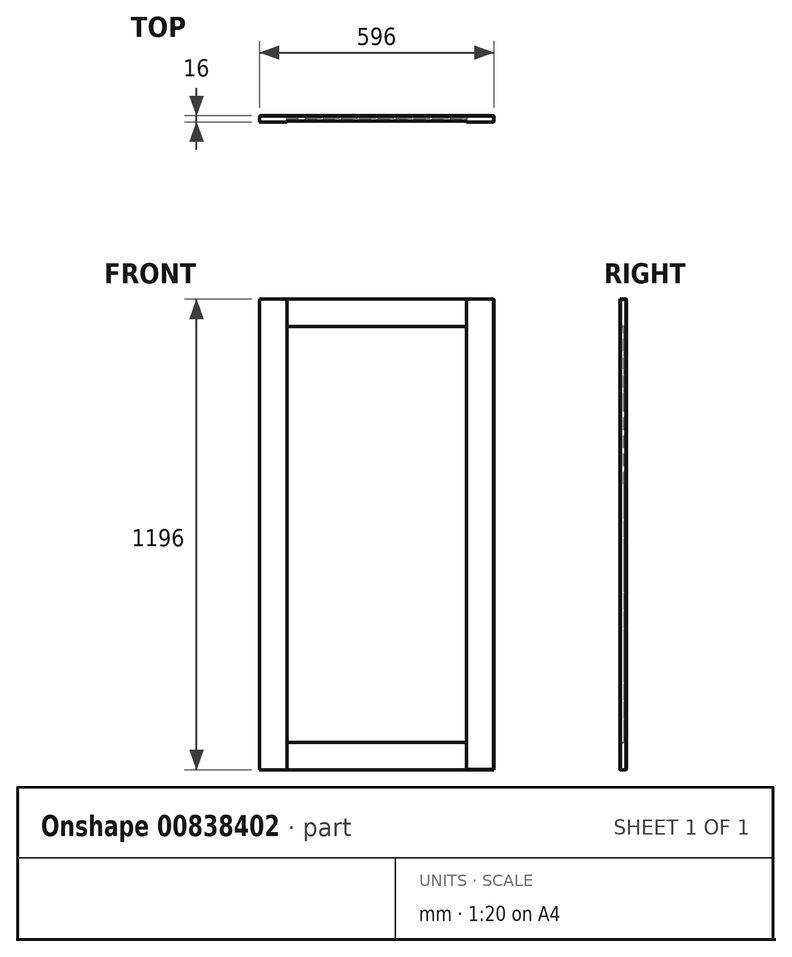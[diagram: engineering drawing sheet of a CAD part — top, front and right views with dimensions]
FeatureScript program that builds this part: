
annotation { "Feature Type Name" : "Feature", "Feature Type Description" : "" }
export const myFeature = defineFeature(function(context is Context, id is Id, definition is map)
    precondition{}
    {
        {
            var Q0;
            Q0=qCreatedBy(makeId("Front.planeOp"),FACE);
            var sketch = newSketch(context, id + "F0", { "sketchPlane" : qUnion([Q0])});
            skLineSegment(sketch, "E0.bottom", {"start": v(0, 0) * mm, "end": v(35.9, 0) * mm});
            skLineSegment(sketch, "E0.top", {"start": v(0, 30.12) * mm, "end": v(35.9, 30.12) * mm});
            skLineSegment(sketch, "E0.left", {"start": v(0, 0) * mm, "end": v(0, 30.12) * mm});
            skLineSegment(sketch, "E0.right", {"start": v(35.9, 0) * mm, "end": v(35.9, 30.12) * mm});
            skSolve(sketch);
        }
        {
            var Q0;
            Q0=makeQuery(id+"F0.imprint","IMPRINT",FACE,{"disambiguationData":[TD([[makeQuery(id+"F0.imprint","IMPRINT",EDGE,{"derivedFrom":sQuery(id+"F0.wireOp",EDGE,"E0.bottom")}),1.0]])]});
            extrude(context, id + "F1", {"entities" : qUnion([Q0]), "depth" : 16 * mm, "offsetDistance" : 25.4 * mm});
        }
        {
            var Q0;
            Q0=makeQuery(id+"F1.opExtrude","SWEPT_FACE",FACE,{"disambiguationData":[OSD([sQuery(id+"F0.wireOp",EDGE,"E0.left")])]});
            extrude(context, id + "F2", {"entities" : qUnion([Q0]), "operationType" : NewBodyOperationType.ADD, "oppositeDirection" : true, "depth" : 196 * mm, "offsetDistance" : 25 * mm});
        }
        {
            var Q0;
            {var subQ0=sQuery(id+"F0.wireOp",EDGE,"E0.bottom");Q0=makeQuery(id+"F2.boolean.opBoolean","MERGE",FACE,{"derivedFrom":[makeQuery(id+"F1.opExtrude","SWEPT_FACE",FACE,{"disambiguationData":[OSD([subQ0])]}),makeQuery(id+"F2.opExtrude","SWEPT_FACE",FACE,{"disambiguationData":[OSD([subQ0,sQuery(id+"F0.wireOp",EDGE,"E0.left")])]})]});}
            extrude(context, id + "F3", {"entities" : qUnion([Q0]), "operationType" : NewBodyOperationType.ADD, "oppositeDirection" : true, "depth" : 796 * mm, "offsetDistance" : 25 * mm});
        }
        {
            var Q0;
            {var subQ0=sQuery(id+"F0.wireOp",EDGE,"E0.left");var subQ1=sQuery(id+"F0.wireOp",EDGE,"E0.bottom");Q0=makeQuery(id+"F3.boolean.opBoolean","MERGE",FACE,{"derivedFrom":[makeQuery(id+"F2.boolean.opBoolean","MERGE",FACE,{"derivedFrom":[makeQuery(id+"F1.opExtrude","CAP_FACE",FACE,{"disambiguationData":[OSD([subQ1,sQuery(id+"F0.wireOp",EDGE,"E0.top"),subQ0,sQuery(id+"F0.wireOp",EDGE,"E0.right")])],"isStart":false}),makeQuery(id+"F2.opExtrude","SWEPT_FACE",FACE,{"disambiguationData":[OSD([subQ0]),TDD([makeQuery(id+"F1.opExtrude","CAP_EDGE",EDGE,{"disambiguationData":[OSD([subQ0])],"isStart":false})])]})]}),makeQuery(id+"F3.opExtrude","SWEPT_FACE",FACE,{"disambiguationData":[OSD([subQ1,subQ0]),TDD([makeQuery(id+"F2.boolean.opBoolean","MERGE",EDGE,{"derivedFrom":[makeQuery(id+"F1.opExtrude","CAP_EDGE",EDGE,{"disambiguationData":[OSD([subQ1])],"isStart":false}),makeQuery(id+"F2.opExtrude","SWEPT_EDGE",EDGE,{"disambiguationData":[OSD([subQ1,subQ0]),TDD([makeQuery(id+"F1.opExtrude","CAP_VERTEX",VERTEX,{"disambiguationData":[OSD([subQ1,subQ0])],"isStart":false})])]})]})])]})]});}
            var sketch = newSketch(context, id + "F4", { "sketchPlane" : qUnion([Q0])});
            skLineSegment(sketch, "E1.bottom", {"start": v(0, 796) * mm, "end": v(42.19, 796) * mm});
            skLineSegment(sketch, "E1.top", {"start": v(0, 751.57) * mm, "end": v(42.19, 751.57) * mm});
            skLineSegment(sketch, "E1.left", {"start": v(0, 796) * mm, "end": v(0, 751.57) * mm});
            skLineSegment(sketch, "E1.right", {"start": v(42.19, 796) * mm, "end": v(42.19, 751.57) * mm});
            skLineSegment(sketch, "E2.bottom", {"start": v(196, 796) * mm, "end": v(153.6, 796) * mm});
            skLineSegment(sketch, "E2.top", {"start": v(196, 746.75) * mm, "end": v(153.6, 746.75) * mm});
            skLineSegment(sketch, "E2.left", {"start": v(196, 796) * mm, "end": v(196, 746.75) * mm});
            skLineSegment(sketch, "E2.right", {"start": v(153.6, 796) * mm, "end": v(153.6, 746.75) * mm});
            skSolve(sketch);
        }
        {
            var Q0;
            Q0=makeQuery(id+"F4.imprint","IMPRINT",FACE,{"disambiguationData":[TD([[makeQuery(id+"F4.imprint","IMPRINT",EDGE,{"derivedFrom":sQuery(id+"F4.wireOp",EDGE,"E1.bottom")}),-1.0]])]});
            var Q1;
            Q1=makeQuery(id+"F4.imprint","IMPRINT",FACE,{"disambiguationData":[TD([[makeQuery(id+"F4.imprint","IMPRINT",EDGE,{"derivedFrom":sQuery(id+"F4.wireOp",EDGE,"E2.bottom")}),-1.0]])]});
            extrude(context, id + "F5", {"entities" : qUnion([Q0, Q1]), "operationType" : NewBodyOperationType.ADD, "depth" : 25 * mm, "offsetDistance" : 25 * mm});
        }
        {
            var Q0;
            {var subQ0=sQuery(id+"F0.wireOp",EDGE,"E0.left");var subQ1=sQuery(id+"F0.wireOp",EDGE,"E0.bottom");Q0=makeQuery(id+"F3.boolean.opBoolean","MERGE",FACE,{"derivedFrom":[makeQuery(id+"F2.boolean.opBoolean","MERGE",FACE,{"derivedFrom":[makeQuery(id+"F1.opExtrude","CAP_FACE",FACE,{"disambiguationData":[OSD([subQ1,sQuery(id+"F0.wireOp",EDGE,"E0.top"),subQ0,sQuery(id+"F0.wireOp",EDGE,"E0.right")])],"isStart":false}),makeQuery(id+"F2.opExtrude","SWEPT_FACE",FACE,{"disambiguationData":[OSD([subQ0]),TDD([makeQuery(id+"F1.opExtrude","CAP_EDGE",EDGE,{"disambiguationData":[OSD([subQ0])],"isStart":false})])]})]}),makeQuery(id+"F3.opExtrude","SWEPT_FACE",FACE,{"disambiguationData":[OSD([subQ1,subQ0]),TDD([makeQuery(id+"F2.boolean.opBoolean","MERGE",EDGE,{"derivedFrom":[makeQuery(id+"F1.opExtrude","CAP_EDGE",EDGE,{"disambiguationData":[OSD([subQ1])],"isStart":false}),makeQuery(id+"F2.opExtrude","SWEPT_EDGE",EDGE,{"disambiguationData":[OSD([subQ1,subQ0]),TDD([makeQuery(id+"F1.opExtrude","CAP_VERTEX",VERTEX,{"disambiguationData":[OSD([subQ1,subQ0])],"isStart":false})])]})]})])]})]});}
            var sketch = newSketch(context, id + "F6", { "sketchPlane" : qUnion([Q0])});
            skLineSegment(sketch, "E3.bottom", {"start": v(196, 0) * mm, "end": v(163.38, 0) * mm});
            skLineSegment(sketch, "E3.top", {"start": v(196, 46.55) * mm, "end": v(163.38, 46.55) * mm});
            skLineSegment(sketch, "E3.left", {"start": v(196, 0) * mm, "end": v(196, 46.55) * mm});
            skLineSegment(sketch, "E3.right", {"start": v(163.38, 0) * mm, "end": v(163.38, 46.55) * mm});
            skLineSegment(sketch, "E4.bottom", {"start": v(0, 0) * mm, "end": v(50.28, 0) * mm});
            skLineSegment(sketch, "E4.top", {"start": v(0, 44.4) * mm, "end": v(50.28, 44.4) * mm});
            skLineSegment(sketch, "E4.left", {"start": v(0, 0) * mm, "end": v(0, 44.4) * mm});
            skLineSegment(sketch, "E4.right", {"start": v(50.28, 0) * mm, "end": v(50.28, 44.4) * mm});
            skSolve(sketch);
        }
        {
            var Q0;
            Q0=makeQuery(id+"F6.imprint","IMPRINT",FACE,{"disambiguationData":[TD([[makeQuery(id+"F6.imprint","IMPRINT",EDGE,{"derivedFrom":sQuery(id+"F6.wireOp",EDGE,"E3.bottom")}),1.0]])]});
            var Q1;
            Q1=makeQuery(id+"F6.imprint","IMPRINT",FACE,{"disambiguationData":[TD([[makeQuery(id+"F6.imprint","IMPRINT",EDGE,{"derivedFrom":sQuery(id+"F6.wireOp",EDGE,"E4.bottom")}),1.0]])]});
            extrude(context, id + "F7", {"entities" : qUnion([Q0, Q1]), "operationType" : NewBodyOperationType.ADD, "depth" : 25 * mm, "offsetDistance" : 25 * mm});
        }
        {
            var Q0;
            Q0=makeQuery(id+"F7.opExtrude","SWEPT_FACE",FACE,{"disambiguationData":[OSD([sQuery(id+"F6.wireOp",EDGE,"E4.right")])]});
            extrude(context, id + "F8", {"entities" : qUnion([Q0]), "operationType" : NewBodyOperationType.ADD, "depth" : 19.72 * mm, "offsetDistance" : 25 * mm});
        }
        {
            var Q0;
            {var subQ0=sQuery(id+"F6.wireOp",EDGE,"E4.top");Q0=makeQuery(id+"F8.boolean.opBoolean","MERGE",FACE,{"derivedFrom":[makeQuery(id+"F7.opExtrude","SWEPT_FACE",FACE,{"disambiguationData":[OSD([subQ0])]}),makeQuery(id+"F8.opExtrude","SWEPT_FACE",FACE,{"disambiguationData":[OSD([subQ0,sQuery(id+"F6.wireOp",EDGE,"E4.right")])]})]});}
            extrude(context, id + "F9", {"entities" : qUnion([Q0]), "operationType" : NewBodyOperationType.ADD, "depth" : 25.6 * mm, "offsetDistance" : 25 * mm});
        }
        {
            var Q0;
            Q0=makeQuery(id+"F7.opExtrude","SWEPT_FACE",FACE,{"disambiguationData":[OSD([sQuery(id+"F6.wireOp",EDGE,"E3.right")])]});
            extrude(context, id + "F10", {"entities" : qUnion([Q0]), "operationType" : NewBodyOperationType.ADD, "depth" : 37.38 * mm, "offsetDistance" : 25 * mm});
        }
        {
            var Q0;
            {var subQ0=sQuery(id+"F6.wireOp",EDGE,"E3.top");Q0=makeQuery(id+"F10.boolean.opBoolean","MERGE",FACE,{"derivedFrom":[makeQuery(id+"F7.opExtrude","SWEPT_FACE",FACE,{"disambiguationData":[OSD([subQ0])]}),makeQuery(id+"F10.opExtrude","SWEPT_FACE",FACE,{"disambiguationData":[OSD([subQ0,sQuery(id+"F6.wireOp",EDGE,"E3.right")])]})]});}
            extrude(context, id + "F11", {"entities" : qUnion([Q0]), "operationType" : NewBodyOperationType.ADD, "depth" : 23.45 * mm, "offsetDistance" : 25 * mm});
        }
        {
            var Q0;
            Q0=makeQuery(id+"F5.opExtrude","SWEPT_FACE",FACE,{"disambiguationData":[OSD([sQuery(id+"F4.wireOp",EDGE,"E1.right")])]});
            extrude(context, id + "F12", {"entities" : qUnion([Q0]), "operationType" : NewBodyOperationType.ADD, "depth" : 27.8 * mm, "offsetDistance" : 25 * mm});
        }
        {
            var Q0;
            {var subQ0=sQuery(id+"F4.wireOp",EDGE,"E1.top");Q0=makeQuery(id+"F12.boolean.opBoolean","MERGE",FACE,{"derivedFrom":[makeQuery(id+"F5.opExtrude","SWEPT_FACE",FACE,{"disambiguationData":[OSD([subQ0])]}),makeQuery(id+"F12.opExtrude","SWEPT_FACE",FACE,{"disambiguationData":[OSD([subQ0,sQuery(id+"F4.wireOp",EDGE,"E1.right")])]})]});}
            extrude(context, id + "F13", {"entities" : qUnion([Q0]), "operationType" : NewBodyOperationType.ADD, "depth" : 25.57 * mm, "offsetDistance" : 25 * mm});
        }
        {
            var Q0;
            Q0=makeQuery(id+"F5.opExtrude","SWEPT_FACE",FACE,{"disambiguationData":[OSD([sQuery(id+"F4.wireOp",EDGE,"E2.top")])]});
            extrude(context, id + "F14", {"entities" : qUnion([Q0]), "operationType" : NewBodyOperationType.ADD, "depth" : 20.75 * mm, "offsetDistance" : 25 * mm});
        }
        {
            var Q0;
            {var subQ0=sQuery(id+"F4.wireOp",EDGE,"E2.right");Q0=makeQuery(id+"F14.boolean.opBoolean","MERGE",FACE,{"derivedFrom":[makeQuery(id+"F5.opExtrude","SWEPT_FACE",FACE,{"disambiguationData":[OSD([subQ0])]}),makeQuery(id+"F14.opExtrude","SWEPT_FACE",FACE,{"disambiguationData":[OSD([sQuery(id+"F4.wireOp",EDGE,"E2.top"),subQ0])]})]});}
            extrude(context, id + "F15", {"entities" : qUnion([Q0]), "operationType" : NewBodyOperationType.ADD, "depth" : 27.6 * mm, "offsetDistance" : 25 * mm});
        }
        {
            var Q0;
            {var subQ0=sQuery(id+"F0.wireOp",EDGE,"E0.left");var subQ1=sQuery(id+"F0.wireOp",EDGE,"E0.bottom");Q0=makeQuery(id+"F3.boolean.opBoolean","MERGE",FACE,{"derivedFrom":[makeQuery(id+"F2.boolean.opBoolean","MERGE",FACE,{"derivedFrom":[makeQuery(id+"F1.opExtrude","CAP_FACE",FACE,{"disambiguationData":[OSD([subQ1,sQuery(id+"F0.wireOp",EDGE,"E0.top"),subQ0,sQuery(id+"F0.wireOp",EDGE,"E0.right")])],"isStart":false}),makeQuery(id+"F2.opExtrude","SWEPT_FACE",FACE,{"disambiguationData":[OSD([subQ0]),TDD([makeQuery(id+"F1.opExtrude","CAP_EDGE",EDGE,{"disambiguationData":[OSD([subQ0])],"isStart":false})])]})]}),makeQuery(id+"F3.opExtrude","SWEPT_FACE",FACE,{"disambiguationData":[OSD([subQ1,subQ0]),TDD([makeQuery(id+"F2.boolean.opBoolean","MERGE",EDGE,{"derivedFrom":[makeQuery(id+"F1.opExtrude","CAP_EDGE",EDGE,{"disambiguationData":[OSD([subQ1])],"isStart":false}),makeQuery(id+"F2.opExtrude","SWEPT_EDGE",EDGE,{"disambiguationData":[OSD([subQ1,subQ0]),TDD([makeQuery(id+"F1.opExtrude","CAP_VERTEX",VERTEX,{"disambiguationData":[OSD([subQ1,subQ0])],"isStart":false})])]})]})])]})]});}
            var sketch = newSketch(context, id + "F16", { "sketchPlane" : qUnion([Q0])});
            skLineSegment(sketch, "E5.bottom", {"start": v(70, 726) * mm, "end": v(126, 726) * mm});
            skLineSegment(sketch, "E5.top", {"start": v(70, 70) * mm, "end": v(126, 70) * mm});
            skLineSegment(sketch, "E5.left", {"start": v(70, 726) * mm, "end": v(70, 70) * mm});
            skLineSegment(sketch, "E5.right", {"start": v(126, 726) * mm, "end": v(126, 70) * mm});
            skSolve(sketch);
        }
        {
            var Q0;
            Q0=makeQuery(id+"F16.imprint","IMPRINT",FACE,{"disambiguationData":[TD([[makeQuery(id+"F16.imprint","IMPRINT",EDGE,{"derivedFrom":sQuery(id+"F16.wireOp",EDGE,"E5.top")}),1.0]])]});
            extrude(context, id + "F17", {"entities" : qUnion([Q0]), "operationType" : NewBodyOperationType.REMOVE, "oppositeDirection" : true, "depth" : 10 * mm, "offsetDistance" : 25 * mm});
        }
        {
            var Q0;
            {var subQ2=sQuery(id+"F0.wireOp",EDGE,"E0.left");var subQ3=sQuery(id+"F0.wireOp",EDGE,"E0.bottom");var subQ4=makeQuery(id+"F1.opExtrude","CAP_FACE",FACE,{"disambiguationData":[OSD([subQ3,sQuery(id+"F0.wireOp",EDGE,"E0.top"),subQ2,sQuery(id+"F0.wireOp",EDGE,"E0.right")])],"isStart":false});var subQ7=makeQuery(id+"F3.opExtrude","SWEPT_FACE",FACE,{"disambiguationData":[OSD([subQ3,subQ2]),TDD([makeQuery(id+"F2.boolean.opBoolean","MERGE",EDGE,{"derivedFrom":[makeQuery(id+"F1.opExtrude","CAP_EDGE",EDGE,{"disambiguationData":[OSD([subQ3])],"isStart":false}),makeQuery(id+"F2.opExtrude","SWEPT_EDGE",EDGE,{"disambiguationData":[OSD([subQ3,subQ2]),TDD([makeQuery(id+"F1.opExtrude","CAP_VERTEX",VERTEX,{"disambiguationData":[OSD([subQ3,subQ2])],"isStart":false})])]})]})])]});var subQ8=makeQuery(id+"F2.opExtrude","SWEPT_FACE",FACE,{"disambiguationData":[OSD([subQ2]),TDD([makeQuery(id+"F1.opExtrude","CAP_EDGE",EDGE,{"disambiguationData":[OSD([subQ2])],"isStart":false})])]});Q0=makeQuery(id+"F17.boolean.opBoolean","SPLIT",FACE,{"disambiguationData":[TD([makeQuery(id+"F1.opExtrude","SWEPT_FACE",FACE,{"disambiguationData":[OSD([subQ3])]})])],"derivedFrom":makeQuery(id+"F3.boolean.opBoolean","MERGE",FACE,{"derivedFrom":[makeQuery(id+"F2.boolean.opBoolean","MERGE",FACE,{"derivedFrom":[subQ4,subQ8]}),subQ7]})});}
            var Q1;
            {var subQ2=sQuery(id+"F4.wireOp",EDGE,"E1.bottom");var subQ3=sQuery(id+"F0.wireOp",EDGE,"E0.left");var subQ4=sQuery(id+"F0.wireOp",EDGE,"E0.bottom");var subQ6=makeQuery(id+"F1.opExtrude","CAP_FACE",FACE,{"disambiguationData":[OSD([subQ4,sQuery(id+"F0.wireOp",EDGE,"E0.top"),subQ3,sQuery(id+"F0.wireOp",EDGE,"E0.right")])],"isStart":false});var subQ7=makeQuery(id+"F2.opExtrude","SWEPT_FACE",FACE,{"disambiguationData":[OSD([subQ3]),TDD([makeQuery(id+"F1.opExtrude","CAP_EDGE",EDGE,{"disambiguationData":[OSD([subQ3])],"isStart":false})])]});var subQ8=makeQuery(id+"F3.opExtrude","SWEPT_FACE",FACE,{"disambiguationData":[OSD([subQ4,subQ3]),TDD([makeQuery(id+"F2.boolean.opBoolean","MERGE",EDGE,{"derivedFrom":[makeQuery(id+"F1.opExtrude","CAP_EDGE",EDGE,{"disambiguationData":[OSD([subQ4])],"isStart":false}),makeQuery(id+"F2.opExtrude","SWEPT_EDGE",EDGE,{"disambiguationData":[OSD([subQ4,subQ3]),TDD([makeQuery(id+"F1.opExtrude","CAP_VERTEX",VERTEX,{"disambiguationData":[OSD([subQ4,subQ3])],"isStart":false})])]})]})])]});Q1=makeQuery(id+"F17.boolean.opBoolean","SPLIT",FACE,{"disambiguationData":[TD([makeQuery(id+"F5.opExtrude","SWEPT_FACE",FACE,{"disambiguationData":[OSD([subQ2])]})])],"derivedFrom":makeQuery(id+"F3.boolean.opBoolean","MERGE",FACE,{"derivedFrom":[makeQuery(id+"F2.boolean.opBoolean","MERGE",FACE,{"derivedFrom":[subQ6,subQ7]}),subQ8]})});}
            extrude(context, id + "F18", {"entities" : qUnion([Q0, Q1]), "operationType" : NewBodyOperationType.REMOVE, "oppositeDirection" : true, "depth" : 2 * mm, "offsetDistance" : 25 * mm});
        }
        {
            var Q0;
            {var subQ0=sQuery(id+"F4.wireOp",EDGE,"E1.right");var subQ1=sQuery(id+"F4.wireOp",EDGE,"E1.top");Q0=makeQuery(id+"F13.boolean.opBoolean","MERGE",FACE,{"derivedFrom":[makeQuery(id+"F12.boolean.opBoolean","MERGE",FACE,{"derivedFrom":[makeQuery(id+"F5.opExtrude","CAP_FACE",FACE,{"disambiguationData":[OSD([sQuery(id+"F4.wireOp",EDGE,"E1.bottom"),subQ1,sQuery(id+"F4.wireOp",EDGE,"E1.left"),subQ0])],"isStart":false}),makeQuery(id+"F12.opExtrude","SWEPT_FACE",FACE,{"disambiguationData":[OSD([subQ0]),TDD([makeQuery(id+"F5.opExtrude","CAP_EDGE",EDGE,{"disambiguationData":[OSD([subQ0])],"isStart":false})])]})]}),makeQuery(id+"F13.opExtrude","SWEPT_FACE",FACE,{"disambiguationData":[OSD([subQ1,subQ0]),TDD([makeQuery(id+"F12.boolean.opBoolean","MERGE",EDGE,{"derivedFrom":[makeQuery(id+"F5.opExtrude","CAP_EDGE",EDGE,{"disambiguationData":[OSD([subQ1])],"isStart":false}),makeQuery(id+"F12.opExtrude","SWEPT_EDGE",EDGE,{"disambiguationData":[OSD([subQ1,subQ0]),TDD([makeQuery(id+"F5.opExtrude","CAP_VERTEX",VERTEX,{"disambiguationData":[OSD([subQ1,subQ0])],"isStart":false})])]})]})])]})]});}
            var Q1;
            {var subQ0=sQuery(id+"F4.wireOp",EDGE,"E2.right");var subQ1=sQuery(id+"F4.wireOp",EDGE,"E2.top");Q1=makeQuery(id+"F15.boolean.opBoolean","MERGE",FACE,{"derivedFrom":[makeQuery(id+"F14.boolean.opBoolean","MERGE",FACE,{"derivedFrom":[makeQuery(id+"F5.opExtrude","CAP_FACE",FACE,{"disambiguationData":[OSD([sQuery(id+"F4.wireOp",EDGE,"E2.bottom"),subQ1,sQuery(id+"F4.wireOp",EDGE,"E2.left"),subQ0])],"isStart":false}),makeQuery(id+"F14.opExtrude","SWEPT_FACE",FACE,{"disambiguationData":[OSD([subQ1]),TDD([makeQuery(id+"F5.opExtrude","CAP_EDGE",EDGE,{"disambiguationData":[OSD([subQ1])],"isStart":false})])]})]}),makeQuery(id+"F15.opExtrude","SWEPT_FACE",FACE,{"disambiguationData":[OSD([subQ1,subQ0]),TDD([makeQuery(id+"F14.boolean.opBoolean","MERGE",EDGE,{"derivedFrom":[makeQuery(id+"F5.opExtrude","CAP_EDGE",EDGE,{"disambiguationData":[OSD([subQ0])],"isStart":false}),makeQuery(id+"F14.opExtrude","SWEPT_EDGE",EDGE,{"disambiguationData":[OSD([subQ1,subQ0]),TDD([makeQuery(id+"F5.opExtrude","CAP_VERTEX",VERTEX,{"disambiguationData":[OSD([subQ1,subQ0])],"isStart":false})])]})]})])]})]});}
            var Q2;
            {var subQ0=sQuery(id+"F6.wireOp",EDGE,"E4.right");var subQ1=sQuery(id+"F6.wireOp",EDGE,"E4.top");Q2=makeQuery(id+"F9.boolean.opBoolean","MERGE",FACE,{"derivedFrom":[makeQuery(id+"F8.boolean.opBoolean","MERGE",FACE,{"derivedFrom":[makeQuery(id+"F7.opExtrude","CAP_FACE",FACE,{"disambiguationData":[OSD([sQuery(id+"F6.wireOp",EDGE,"E4.bottom"),subQ1,sQuery(id+"F6.wireOp",EDGE,"E4.left"),subQ0])],"isStart":false}),makeQuery(id+"F8.opExtrude","SWEPT_FACE",FACE,{"disambiguationData":[OSD([subQ0]),TDD([makeQuery(id+"F7.opExtrude","CAP_EDGE",EDGE,{"disambiguationData":[OSD([subQ0])],"isStart":false})])]})]}),makeQuery(id+"F9.opExtrude","SWEPT_FACE",FACE,{"disambiguationData":[OSD([subQ1,subQ0]),TDD([makeQuery(id+"F8.boolean.opBoolean","MERGE",EDGE,{"derivedFrom":[makeQuery(id+"F7.opExtrude","CAP_EDGE",EDGE,{"disambiguationData":[OSD([subQ1])],"isStart":false}),makeQuery(id+"F8.opExtrude","SWEPT_EDGE",EDGE,{"disambiguationData":[OSD([subQ1,subQ0]),TDD([makeQuery(id+"F7.opExtrude","CAP_VERTEX",VERTEX,{"disambiguationData":[OSD([subQ1,subQ0])],"isStart":false})])]})]})])]})]});}
            var Q3;
            {var subQ0=sQuery(id+"F6.wireOp",EDGE,"E3.right");var subQ1=sQuery(id+"F6.wireOp",EDGE,"E3.top");Q3=makeQuery(id+"F11.boolean.opBoolean","MERGE",FACE,{"derivedFrom":[makeQuery(id+"F10.boolean.opBoolean","MERGE",FACE,{"derivedFrom":[makeQuery(id+"F7.opExtrude","CAP_FACE",FACE,{"disambiguationData":[OSD([sQuery(id+"F6.wireOp",EDGE,"E3.bottom"),subQ1,sQuery(id+"F6.wireOp",EDGE,"E3.left"),subQ0])],"isStart":false}),makeQuery(id+"F10.opExtrude","SWEPT_FACE",FACE,{"disambiguationData":[OSD([subQ0]),TDD([makeQuery(id+"F7.opExtrude","CAP_EDGE",EDGE,{"disambiguationData":[OSD([subQ0])],"isStart":false})])]})]}),makeQuery(id+"F11.opExtrude","SWEPT_FACE",FACE,{"disambiguationData":[OSD([subQ1,subQ0]),TDD([makeQuery(id+"F10.boolean.opBoolean","MERGE",EDGE,{"derivedFrom":[makeQuery(id+"F7.opExtrude","CAP_EDGE",EDGE,{"disambiguationData":[OSD([subQ1])],"isStart":false}),makeQuery(id+"F10.opExtrude","SWEPT_EDGE",EDGE,{"disambiguationData":[OSD([subQ1,subQ0]),TDD([makeQuery(id+"F7.opExtrude","CAP_VERTEX",VERTEX,{"disambiguationData":[OSD([subQ1,subQ0])],"isStart":false})])]})]})])]})]});}
            extrude(context, id + "F19", {"entities" : qUnion([Q0, Q1, Q2, Q3]), "operationType" : NewBodyOperationType.REMOVE, "oppositeDirection" : true, "depth" : 25 * mm, "offsetDistance" : 25 * mm});
        }
        {
            var Q0;
            {var subQ0=sQuery(id+"F4.wireOp",EDGE,"E2.left");var subQ1=sQuery(id+"F0.wireOp",EDGE,"E0.left");var subQ2=sQuery(id+"F0.wireOp",EDGE,"E0.bottom");var subQ3=sQuery(id+"F6.wireOp",EDGE,"E3.left");Q0=makeQuery(id+"F14.boolean.opBoolean","MERGE",FACE,{"derivedFrom":[makeQuery(id+"F11.boolean.opBoolean","MERGE",FACE,{"derivedFrom":[makeQuery(id+"F7.boolean.opBoolean","MERGE",FACE,{"derivedFrom":[makeQuery(id+"F5.boolean.opBoolean","MERGE",FACE,{"derivedFrom":[makeQuery(id+"F3.boolean.opBoolean","MERGE",FACE,{"derivedFrom":[makeQuery(id+"F2.opExtrude","CAP_FACE",FACE,{"disambiguationData":[OSD([subQ1])],"isStart":false}),makeQuery(id+"F3.opExtrude","SWEPT_FACE",FACE,{"disambiguationData":[OSD([subQ2,subQ1]),TDD([makeQuery(id+"F2.opExtrude","CAP_EDGE",EDGE,{"disambiguationData":[OSD([subQ2,subQ1])],"isStart":false})])]})]}),makeQuery(id+"F5.opExtrude","SWEPT_FACE",FACE,{"disambiguationData":[OSD([subQ0])]})]}),makeQuery(id+"F7.opExtrude","SWEPT_FACE",FACE,{"disambiguationData":[OSD([subQ3])]})]}),makeQuery(id+"F11.opExtrude","SWEPT_FACE",FACE,{"disambiguationData":[OSD([subQ2,subQ1,sQuery(id+"F6.wireOp",EDGE,"E3.top"),subQ3])]})]}),makeQuery(id+"F14.opExtrude","SWEPT_FACE",FACE,{"disambiguationData":[OSD([subQ2,subQ1,sQuery(id+"F4.wireOp",EDGE,"E2.top"),subQ0])]})]});}
            extrude(context, id + "F20", {"entities" : qUnion([Q0]), "operationType" : NewBodyOperationType.ADD, "depth" : 400 * mm, "offsetDistance" : 25 * mm});
        }
        {
            var Q0;
            {var subQ0=sQuery(id+"F6.wireOp",EDGE,"E3.right");var subQ1=sQuery(id+"F6.wireOp",EDGE,"E3.top");Q0=makeQuery(id+"F18.boolean.opBoolean","MERGE",FACE,{"derivedFrom":[makeQuery(id+"F11.boolean.opBoolean","MERGE",FACE,{"derivedFrom":[makeQuery(id+"F10.opExtrude","CAP_FACE",FACE,{"disambiguationData":[OSD([subQ0])],"isStart":false}),makeQuery(id+"F11.opExtrude","SWEPT_FACE",FACE,{"disambiguationData":[OSD([subQ1,subQ0]),TDD([makeQuery(id+"F10.opExtrude","CAP_EDGE",EDGE,{"disambiguationData":[OSD([subQ1,subQ0])],"isStart":false})])]})]}),makeQuery(id+"F17.boolean.opBoolean","COPY",FACE,{"derivedFrom":makeQuery(id+"F17.opExtrude","SWEPT_FACE",FACE,{"disambiguationData":[OSD([sQuery(id+"F16.wireOp",EDGE,"E5.right")])]})}),makeQuery(id+"F18.opExtrude","SWEPT_FACE",FACE,{"disambiguationData":[OSD([subQ1,subQ0])]})]});}
            var Q1;
            {var subQ0=sQuery(id+"F4.wireOp",EDGE,"E2.right");var subQ1=sQuery(id+"F4.wireOp",EDGE,"E2.top");Q1=makeQuery(id+"F18.boolean.opBoolean","MERGE",FACE,{"derivedFrom":[makeQuery(id+"F15.opExtrude","CAP_FACE",FACE,{"disambiguationData":[OSD([subQ1,subQ0])],"isStart":false}),makeQuery(id+"F18.opExtrude","SWEPT_FACE",FACE,{"disambiguationData":[OSD([subQ1,subQ0])]})]});}
            extrude(context, id + "F21", {"entities" : qUnion([Q0, Q1]), "operationType" : NewBodyOperationType.REMOVE, "oppositeDirection" : true, "depth" : 400 * mm, "offsetDistance" : 25 * mm});
        }
        {
            var Q0;
            {var subQ0=sQuery(id+"F4.wireOp",EDGE,"E2.bottom");var subQ1=sQuery(id+"F0.wireOp",EDGE,"E0.left");var subQ2=sQuery(id+"F0.wireOp",EDGE,"E0.bottom");var subQ3=sQuery(id+"F4.wireOp",EDGE,"E1.bottom");Q0=makeQuery(id+"F20.boolean.opBoolean","MERGE",FACE,{"derivedFrom":[makeQuery(id+"F15.boolean.opBoolean","MERGE",FACE,{"derivedFrom":[makeQuery(id+"F12.boolean.opBoolean","MERGE",FACE,{"derivedFrom":[makeQuery(id+"F5.boolean.opBoolean","MERGE",FACE,{"derivedFrom":[makeQuery(id+"F3.opExtrude","CAP_FACE",FACE,{"disambiguationData":[OSD([subQ2,subQ1])],"isStart":false}),makeQuery(id+"F5.opExtrude","SWEPT_FACE",FACE,{"disambiguationData":[OSD([subQ3])]}),makeQuery(id+"F5.opExtrude","SWEPT_FACE",FACE,{"disambiguationData":[OSD([subQ0])]})]}),makeQuery(id+"F12.opExtrude","SWEPT_FACE",FACE,{"disambiguationData":[OSD([subQ2,subQ1,subQ3,sQuery(id+"F4.wireOp",EDGE,"E1.right")])]})]}),makeQuery(id+"F15.opExtrude","SWEPT_FACE",FACE,{"disambiguationData":[OSD([subQ2,subQ1,subQ0,sQuery(id+"F4.wireOp",EDGE,"E2.right")])]})]}),makeQuery(id+"F20.opExtrude","SWEPT_FACE",FACE,{"disambiguationData":[OSD([subQ2,subQ1,subQ0,sQuery(id+"F4.wireOp",EDGE,"E2.left")])]})]});}
            extrude(context, id + "F22", {"entities" : qUnion([Q0]), "operationType" : NewBodyOperationType.ADD, "depth" : 200 * mm, "offsetDistance" : 25 * mm});
        }
        {
            var Q0;
            Q0=makeQuery(id+"F17.boolean.opBoolean","COPY",FACE,{"derivedFrom":makeQuery(id+"F17.opExtrude","SWEPT_FACE",FACE,{"disambiguationData":[OSD([sQuery(id+"F16.wireOp",EDGE,"E5.bottom")])]})});
            var Q1;
            {var subQ0=sQuery(id+"F16.wireOp",EDGE,"E5.right");var subQ1=sQuery(id+"F16.wireOp",EDGE,"E5.bottom");var subQ2=sQuery(id+"F4.wireOp",EDGE,"E2.right");var subQ3=sQuery(id+"F4.wireOp",EDGE,"E2.top");var subQ4=makeQuery(id+"F17.boolean.opBoolean","COPY",EDGE,{"derivedFrom":makeQuery(id+"F17.opExtrude","SWEPT_EDGE",EDGE,{"disambiguationData":[OSD([subQ3,subQ2,subQ1,subQ0])]})});Q1=makeQuery(id+"F21.boolean.opBoolean","COPY",FACE,{"derivedFrom":makeQuery(id+"F21.opExtrude","SWEPT_FACE",FACE,{"disambiguationData":[OSD([subQ3,subQ2,subQ1,subQ0]),TDD([makeQuery(id+"F18.boolean.opBoolean","MERGE",EDGE,{"derivedFrom":[subQ4,makeQuery(id+"F18.opExtrude","SWEPT_EDGE",EDGE,{"disambiguationData":[OSD([subQ3,subQ2,subQ1,subQ0])]})]}),makeQuery(id+"F18.boolean.opBoolean","SPLIT",EDGE,{"derivedFrom":subQ4})])]})});}
            extrude(context, id + "F23", {"entities" : qUnion([Q0, Q1]), "operationType" : NewBodyOperationType.REMOVE, "oppositeDirection" : true, "depth" : 200 * mm, "offsetDistance" : 25 * mm});
        }
        {
            var Q0;
            Q0=makeQuery(id+"F22.opExtrude","CAP_FACE",FACE,{"disambiguationData":[OSD([sQuery(id+"F0.wireOp",EDGE,"E0.bottom"),sQuery(id+"F0.wireOp",EDGE,"E0.left"),sQuery(id+"F4.wireOp",EDGE,"E1.bottom"),sQuery(id+"F4.wireOp",EDGE,"E1.right"),sQuery(id+"F4.wireOp",EDGE,"E2.bottom"),sQuery(id+"F4.wireOp",EDGE,"E2.left"),sQuery(id+"F4.wireOp",EDGE,"E2.right")])],"isStart":false});
            extrude(context, id + "F24", {"entities" : qUnion([Q0]), "operationType" : NewBodyOperationType.ADD, "depth" : 200 * mm, "offsetDistance" : 25 * mm});
        }
        {
            var Q0;
            Q0=makeQuery(id+"F23.boolean.opBoolean","COPY",FACE,{"derivedFrom":makeQuery(id+"F23.opExtrude","CAP_FACE",FACE,{"disambiguationData":[OSD([sQuery(id+"F16.wireOp",EDGE,"E5.bottom")])],"isStart":false})});
            var Q1;
            Q1=makeQuery(id+"F23.boolean.opBoolean","COPY",FACE,{"derivedFrom":makeQuery(id+"F23.opExtrude","CAP_FACE",FACE,{"disambiguationData":[OSD([sQuery(id+"F4.wireOp",EDGE,"E2.top"),sQuery(id+"F4.wireOp",EDGE,"E2.right"),sQuery(id+"F16.wireOp",EDGE,"E5.bottom"),sQuery(id+"F16.wireOp",EDGE,"E5.right")])],"isStart":false})});
            extrude(context, id + "F25", {"entities" : qUnion([Q0, Q1]), "operationType" : NewBodyOperationType.REMOVE, "oppositeDirection" : true, "depth" : 200 * mm, "offsetDistance" : 25 * mm});
        }
        {
            var Q0;
            Q0=makeQuery(id+"F19.boolean.opBoolean","COPY",EDGE,{"derivedFrom":makeQuery(id+"F19.opExtrude","CAP_EDGE",EDGE,{"disambiguationData":[OSD([sQuery(id+"F0.wireOp",EDGE,"E0.bottom"),sQuery(id+"F0.wireOp",EDGE,"E0.left"),sQuery(id+"F6.wireOp",EDGE,"E4.bottom"),sQuery(id+"F6.wireOp",EDGE,"E4.right")])],"isStart":false})});
            var Q1;
            {var subQ0=sQuery(id+"F4.wireOp",EDGE,"E1.left");var subQ1=sQuery(id+"F4.wireOp",EDGE,"E1.bottom");var subQ2=sQuery(id+"F0.wireOp",EDGE,"E0.left");var subQ3=sQuery(id+"F0.wireOp",EDGE,"E0.bottom");Q1=makeQuery(id+"F24.boolean.opBoolean","MERGE",EDGE,{"derivedFrom":[makeQuery(id+"F22.boolean.opBoolean","MERGE",EDGE,{"derivedFrom":[makeQuery(id+"F19.boolean.opBoolean","MERGE",EDGE,{"derivedFrom":[makeQuery(id+"F3.boolean.opBoolean","MERGE",EDGE,{"derivedFrom":[makeQuery(id+"F1.opExtrude","CAP_EDGE",EDGE,{"disambiguationData":[OSD([subQ2])],"isStart":false}),makeQuery(id+"F3.opExtrude","SWEPT_EDGE",EDGE,{"disambiguationData":[OSD([subQ3,subQ2]),TDD([makeQuery(id+"F1.opExtrude","CAP_VERTEX",VERTEX,{"disambiguationData":[OSD([subQ3,subQ2])],"isStart":false})])]})]}),makeQuery(id+"F19.opExtrude","CAP_EDGE",EDGE,{"disambiguationData":[OSD([subQ3,subQ2,sQuery(id+"F6.wireOp",EDGE,"E4.top"),sQuery(id+"F6.wireOp",EDGE,"E4.left")])],"isStart":false}),makeQuery(id+"F19.opExtrude","CAP_EDGE",EDGE,{"disambiguationData":[OSD([subQ3,subQ2,sQuery(id+"F4.wireOp",EDGE,"E1.top"),subQ0])],"isStart":false})]}),makeQuery(id+"F22.opExtrude","SWEPT_EDGE",EDGE,{"disambiguationData":[OSD([subQ1,subQ0])]})]}),makeQuery(id+"F24.opExtrude","SWEPT_EDGE",EDGE,{"disambiguationData":[OSD([subQ1,subQ0])]})]});}
            var Q2;
            {var subQ0=sQuery(id+"F6.wireOp",EDGE,"E3.bottom");Q2=makeQuery(id+"F20.boolean.opBoolean","MERGE",EDGE,{"derivedFrom":[makeQuery(id+"F19.boolean.opBoolean","COPY",EDGE,{"derivedFrom":makeQuery(id+"F19.opExtrude","CAP_EDGE",EDGE,{"disambiguationData":[OSD([sQuery(id+"F0.wireOp",EDGE,"E0.bottom"),sQuery(id+"F0.wireOp",EDGE,"E0.left"),subQ0,sQuery(id+"F6.wireOp",EDGE,"E3.right")])],"isStart":false})}),makeQuery(id+"F20.opExtrude","SWEPT_EDGE",EDGE,{"disambiguationData":[OSD([subQ0,sQuery(id+"F6.wireOp",EDGE,"E3.left")])]})]});}
            var Q3;
            {var subQ0=sQuery(id+"F4.wireOp",EDGE,"E2.left");var subQ1=sQuery(id+"F4.wireOp",EDGE,"E2.bottom");Q3=makeQuery(id+"F24.boolean.opBoolean","MERGE",EDGE,{"derivedFrom":[makeQuery(id+"F22.boolean.opBoolean","MERGE",EDGE,{"derivedFrom":[makeQuery(id+"F20.opExtrude","CAP_EDGE",EDGE,{"disambiguationData":[OSD([sQuery(id+"F0.wireOp",EDGE,"E0.bottom"),sQuery(id+"F0.wireOp",EDGE,"E0.left"),sQuery(id+"F4.wireOp",EDGE,"E2.top"),subQ0,sQuery(id+"F6.wireOp",EDGE,"E3.top"),sQuery(id+"F6.wireOp",EDGE,"E3.left")])],"isStart":false}),makeQuery(id+"F22.opExtrude","SWEPT_EDGE",EDGE,{"disambiguationData":[OSD([subQ1,subQ0])]})]}),makeQuery(id+"F24.opExtrude","SWEPT_EDGE",EDGE,{"disambiguationData":[OSD([subQ1,subQ0])]})]});}
            var Q4;
            Q4=makeQuery(id+"F24.opExtrude","CAP_EDGE",EDGE,{"disambiguationData":[OSD([sQuery(id+"F0.wireOp",EDGE,"E0.bottom"),sQuery(id+"F0.wireOp",EDGE,"E0.left"),sQuery(id+"F4.wireOp",EDGE,"E2.bottom"),sQuery(id+"F4.wireOp",EDGE,"E2.left"),sQuery(id+"F4.wireOp",EDGE,"E2.right")])],"isStart":false});
            var Q5;
            {var subQ0=sQuery(id+"F4.wireOp",EDGE,"E1.right");var subQ1=sQuery(id+"F4.wireOp",EDGE,"E1.bottom");var subQ2=sQuery(id+"F0.wireOp",EDGE,"E0.left");var subQ3=sQuery(id+"F0.wireOp",EDGE,"E0.bottom");Q5=makeQuery(id+"F24.opExtrude","CAP_EDGE",EDGE,{"disambiguationData":[OSD([subQ3,subQ2,subQ1,subQ0]),TDD([makeQuery(id+"F22.opExtrude","CAP_EDGE",EDGE,{"disambiguationData":[OSD([subQ3,subQ2,subQ1,subQ0]),TDD([makeQuery(id+"F19.boolean.opBoolean","COPY",EDGE,{"derivedFrom":makeQuery(id+"F19.opExtrude","CAP_EDGE",EDGE,{"disambiguationData":[OSD([subQ3,subQ2,subQ1,subQ0])],"isStart":false})})])],"isStart":false})])],"isStart":false});}
            var Q6;
            {var subQ0=sQuery(id+"F0.wireOp",EDGE,"E0.left");var subQ1=sQuery(id+"F0.wireOp",EDGE,"E0.bottom");Q6=makeQuery(id+"F24.boolean.opBoolean","MERGE",FACE,{"derivedFrom":[makeQuery(id+"F22.boolean.opBoolean","MERGE",FACE,{"derivedFrom":[makeQuery(id+"F20.boolean.opBoolean","MERGE",FACE,{"derivedFrom":[makeQuery(id+"F3.boolean.opBoolean","MERGE",FACE,{"derivedFrom":[makeQuery(id+"F2.boolean.opBoolean","MERGE",FACE,{"derivedFrom":[makeQuery(id+"F1.opExtrude","CAP_FACE",FACE,{"disambiguationData":[OSD([subQ1,sQuery(id+"F0.wireOp",EDGE,"E0.top"),subQ0,sQuery(id+"F0.wireOp",EDGE,"E0.right")])],"isStart":true}),makeQuery(id+"F2.opExtrude","SWEPT_FACE",FACE,{"disambiguationData":[OSD([subQ0]),TDD([makeQuery(id+"F1.opExtrude","CAP_EDGE",EDGE,{"disambiguationData":[OSD([subQ0])],"isStart":true})])]})]}),makeQuery(id+"F3.opExtrude","SWEPT_FACE",FACE,{"disambiguationData":[OSD([subQ1,subQ0]),TDD([makeQuery(id+"F2.boolean.opBoolean","MERGE",EDGE,{"derivedFrom":[makeQuery(id+"F1.opExtrude","CAP_EDGE",EDGE,{"disambiguationData":[OSD([subQ1])],"isStart":true}),makeQuery(id+"F2.opExtrude","SWEPT_EDGE",EDGE,{"disambiguationData":[OSD([subQ1,subQ0]),TDD([makeQuery(id+"F1.opExtrude","CAP_VERTEX",VERTEX,{"disambiguationData":[OSD([subQ1,subQ0])],"isStart":true})])]})]})])]})]}),makeQuery(id+"F20.opExtrude","SWEPT_FACE",FACE,{"disambiguationData":[OSD([subQ1,subQ0])]})]}),makeQuery(id+"F22.opExtrude","SWEPT_FACE",FACE,{"disambiguationData":[OSD([subQ1,subQ0])]})]}),makeQuery(id+"F24.opExtrude","SWEPT_FACE",FACE,{"disambiguationData":[OSD([subQ1,subQ0])]})]});}
            chamfer(context, id + "F26", {"entities" : qUnion([Q0, Q1, Q2, Q3, Q4, Q5, Q6]), "width" : 1 * mm, "tangentPropagation" : true});
        }
    });
